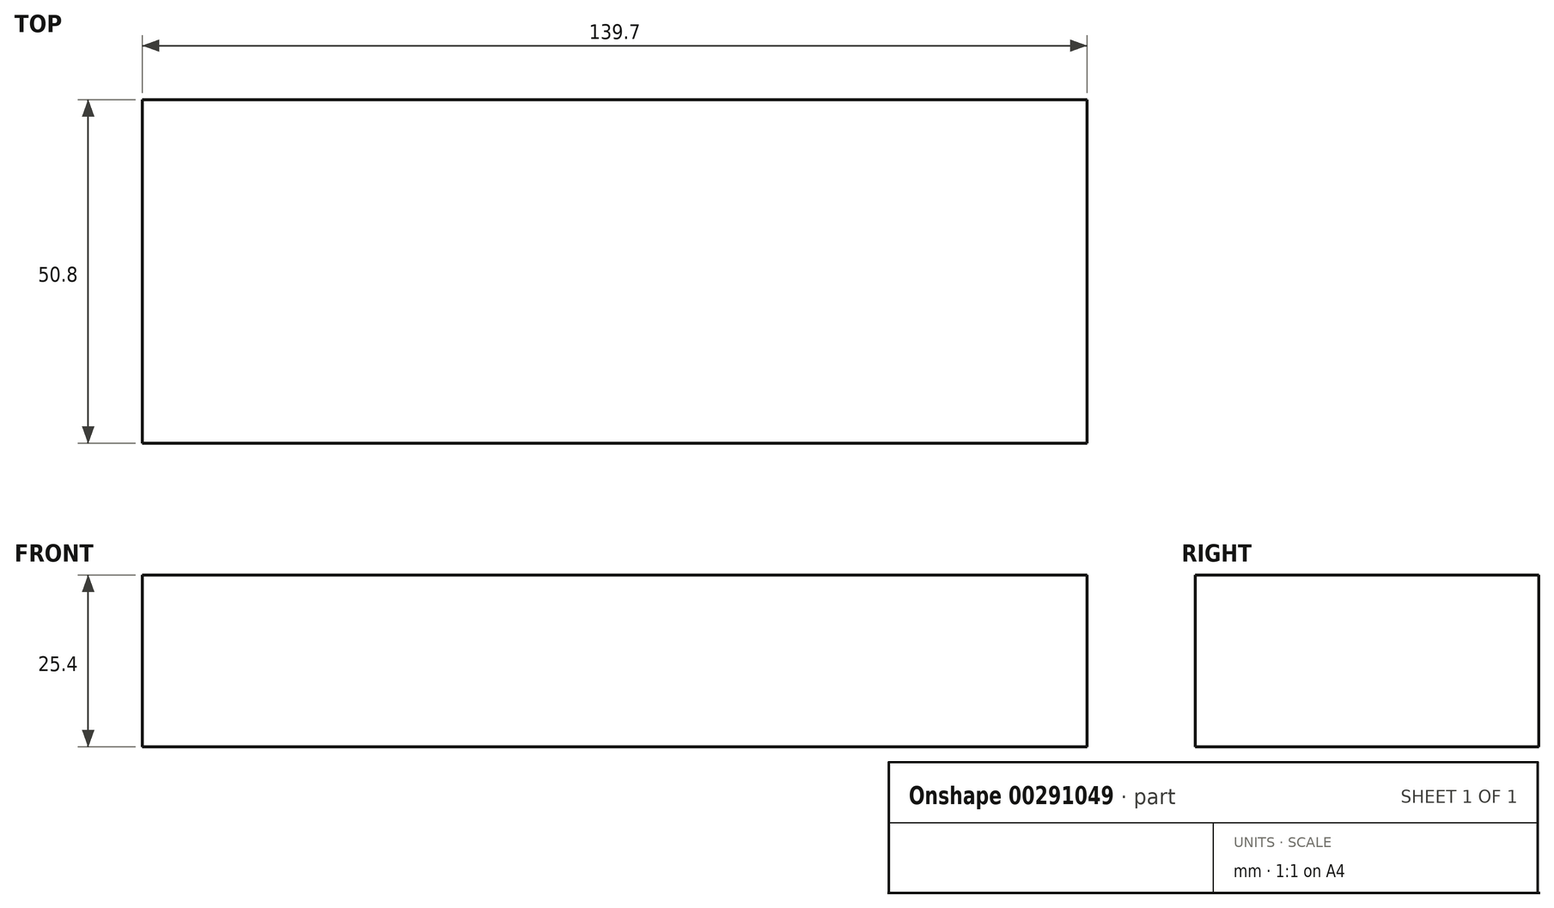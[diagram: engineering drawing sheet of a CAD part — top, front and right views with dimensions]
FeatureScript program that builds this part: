
annotation { "Feature Type Name" : "Feature", "Feature Type Description" : "" }
export const myFeature = defineFeature(function(context is Context, id is Id, definition is map)
    precondition{}
    {
        {
            var Q0;
            Q0=qCreatedBy(makeId("Top.planeOp"),FACE);
            var sketch = newSketch(context, id + "F0", { "sketchPlane" : qUnion([Q0])});
            skLineSegment(sketch, "E0.bottom", {"start": v(-58.14, 22.23) * mm, "end": v(81.56, 22.23) * mm});
            skLineSegment(sketch, "E0.top", {"start": v(-58.14, -28.57) * mm, "end": v(81.56, -28.57) * mm});
            skLineSegment(sketch, "E0.left", {"start": v(-58.14, 22.23) * mm, "end": v(-58.14, -28.57) * mm});
            skLineSegment(sketch, "E0.right", {"start": v(81.56, 22.23) * mm, "end": v(81.56, -28.57) * mm});
            skSolve(sketch);
        }
        {
            var Q0;
            Q0=qSketchRegion(id+"F0",true);
            extrude(context, id + "F1", {"entities" : qUnion([Q0]), "depth" : 25.4 * mm});
        }
    });
